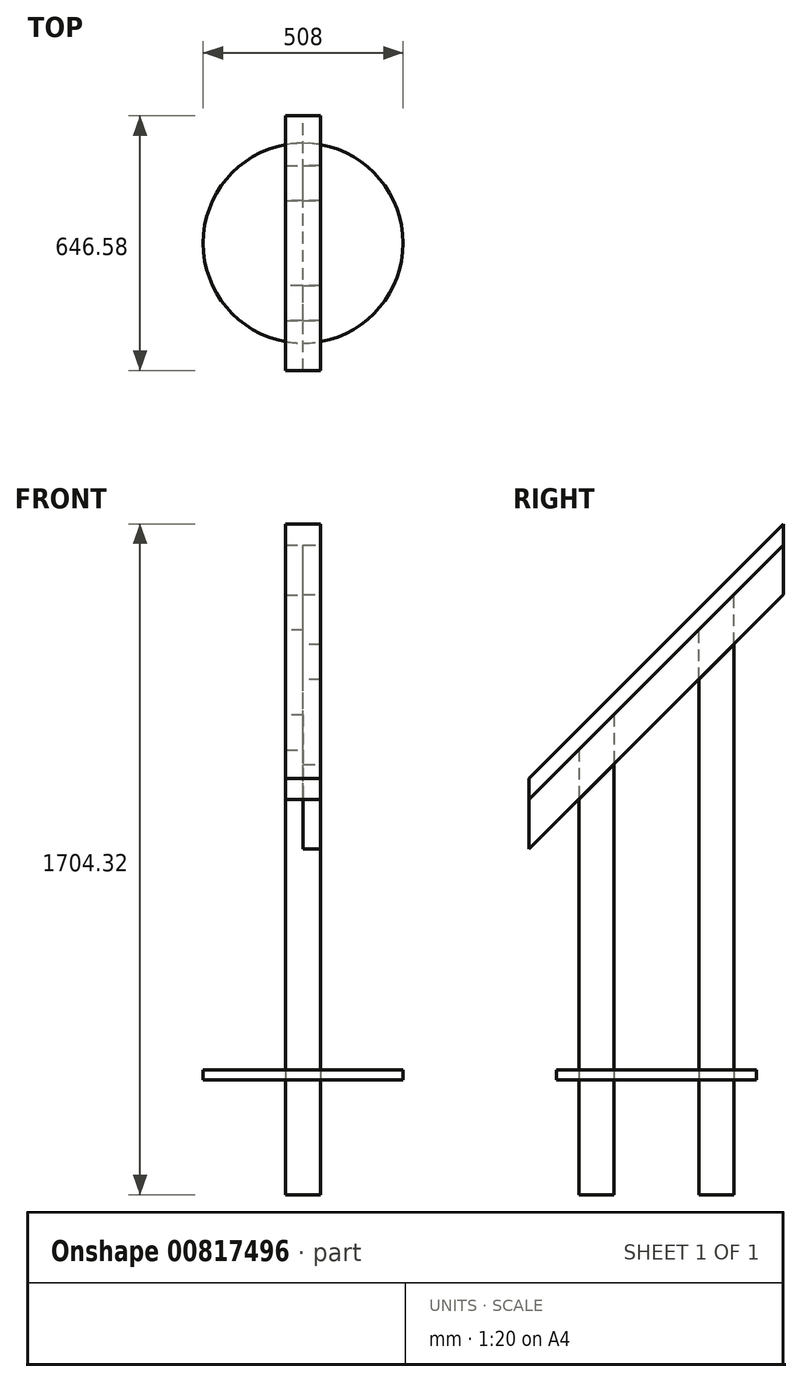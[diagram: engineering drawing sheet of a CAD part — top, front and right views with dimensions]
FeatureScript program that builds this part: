
annotation { "Feature Type Name" : "Feature", "Feature Type Description" : "" }
export const myFeature = defineFeature(function(context is Context, id is Id, definition is map)
    precondition{}
    {
        {
            var Q0;
            Q0=qCreatedBy(makeId("Top.planeOp"),FACE);
            var sketch = newSketch(context, id + "F0", { "sketchPlane" : qUnion([Q0])});
            skCircle(sketch, "E0", {"center": v(0, 0) * mm, "radius": 254 * mm});
            skCircle(sketch, "E1", {"center": v(0, 152.4) * mm, "radius": 62.86 * mm, "construction": true});
            skCircle(sketch, "E2", {"center": v(0, -152.4) * mm, "radius": 62.86 * mm, "construction": true});
            skLineSegment(sketch, "E3.bottom", {"start": v(-44.45, 107.95) * mm, "end": v(44.45, 107.95) * mm});
            skLineSegment(sketch, "E3.top", {"start": v(-44.45, 196.85) * mm, "end": v(44.45, 196.85) * mm});
            skLineSegment(sketch, "E3.left", {"start": v(-44.45, 107.95) * mm, "end": v(-44.45, 196.85) * mm});
            skLineSegment(sketch, "E3.right", {"start": v(44.45, 107.95) * mm, "end": v(44.45, 196.85) * mm});
            skLineSegment(sketch, "E4.bottom", {"start": v(44.45, -107.95) * mm, "end": v(-44.45, -107.95) * mm});
            skLineSegment(sketch, "E4.top", {"start": v(44.45, -196.85) * mm, "end": v(-44.45, -196.85) * mm});
            skLineSegment(sketch, "E4.left", {"start": v(44.45, -107.95) * mm, "end": v(44.45, -196.85) * mm});
            skLineSegment(sketch, "E4.right", {"start": v(-44.45, -107.95) * mm, "end": v(-44.45, -196.85) * mm});
            skCircle(sketch, "E5", {"center": v(0, 0) * mm, "radius": 152.4 * mm, "construction": true});
            skSolve(sketch);
        }
        {
            var Q0;
            Q0=makeQuery(id+"F0.imprint","IMPRINT",FACE,{"disambiguationData":[TD([[makeQuery(id+"F0.imprint","IMPRINT",EDGE,{"derivedFrom":sQuery(id+"F0.wireOp",EDGE,"E3.bottom")}),1.0]])]});
            extrude(context, id + "F1", {"entities" : qUnion([Q0]), "depth" : 1219.2 * mm, "offsetDistance" : 25.4 * mm, "hasSecondDirection" : true, "secondDirectionOppositeDirection" : true, "secondDirectionDepth" : 304.8 * mm});
        }
        {
            var Q0;
            Q0=makeQuery(id+"F0.imprint","IMPRINT",FACE,{"disambiguationData":[TD([[makeQuery(id+"F0.imprint","IMPRINT",EDGE,{"derivedFrom":sQuery(id+"F0.wireOp",EDGE,"E4.bottom")}),1.0]])]});
            extrude(context, id + "F2", {"entities" : qUnion([Q0]), "depth" : 914.4 * mm, "offsetDistance" : 25.4 * mm, "hasSecondDirection" : true, "secondDirectionOppositeDirection" : true, "secondDirectionDepth" : 304.8 * mm});
        }
        {
            var Q0;
            Q0=makeQuery(id+"F0.imprint","IMPRINT",FACE,{"disambiguationData":[TD([[makeQuery(id+"F0.imprint","IMPRINT",EDGE,{"derivedFrom":sQuery(id+"F0.wireOp",EDGE,"E0")}),1.0]])]});
            extrude(context, id + "F3", {"entities" : qUnion([Q0]), "endBound" : BoundingType.SYMMETRIC, "depth" : 25.4 * mm, "offsetDistance" : 25.4 * mm});
        }
        {
            var Q0;
            Q0=qCreatedBy(makeId("Right.planeOp"),FACE);
            var sketch = newSketch(context, id + "F4", { "sketchPlane" : qUnion([Q0])});
            skLineSegment(sketch, "E6.0.0", {"start": v(-196.85, -304.8) * mm, "end": v(-107.95, -304.8) * mm, "construction": true});
            skLineSegment(sketch, "E6.0.1", {"start": v(-107.95, -304.8) * mm, "end": v(-107.95, 914.4) * mm, "construction": true});
            skLineSegment(sketch, "E6.0.2", {"start": v(-107.95, 914.4) * mm, "end": v(-196.85, 914.4) * mm, "construction": true});
            skLineSegment(sketch, "E6.0.3", {"start": v(-196.85, 914.4) * mm, "end": v(-196.85, -304.8) * mm, "construction": true});
            skLineSegment(sketch, "E6.1.0", {"start": v(107.95, -304.8) * mm, "end": v(196.85, -304.8) * mm, "construction": true});
            skLineSegment(sketch, "E6.1.1", {"start": v(196.85, -304.8) * mm, "end": v(196.85, 1219.2) * mm, "construction": true});
            skLineSegment(sketch, "E6.1.2", {"start": v(196.85, 1219.2) * mm, "end": v(107.95, 1219.2) * mm, "construction": true});
            skLineSegment(sketch, "E6.1.3", {"start": v(107.95, 1219.2) * mm, "end": v(107.95, -304.8) * mm, "construction": true});
            skLineSegment(sketch, "E7", {"start": v(-323.29, 699.06) * mm, "end": v(323.29, 1345.64) * mm});
            skArc(sketch, "E8", {"start": v(323.29, 1345.64) * mm, "mid": v(-323.29, 1345.64) * mm, "end": v(-323.29, 699.06) * mm, "construction": true});
            skLineSegment(sketch, "E9", {"start": v(-323.29, 787.96) * mm, "end": v(-323.29, 573.34) * mm, "construction": true});
            skLineSegment(sketch, "E10", {"start": v(-323.29, 573.34) * mm, "end": v(323.29, 1219.92) * mm, "construction": true});
            skLineSegment(sketch, "E11", {"start": v(323.29, 1219.92) * mm, "end": v(323.29, 1434.54) * mm, "construction": true});
            skLineSegment(sketch, "E12", {"start": v(-323.29, 787.96) * mm, "end": v(323.29, 1434.54) * mm, "construction": true});
            skLineSegment(sketch, "E13", {"start": v(323.29, 1399.52) * mm, "end": v(-323.29, 752.94) * mm, "construction": true});
            skSolve(sketch);
        }
        {
            var Q0;
            Q0=qCreatedBy(makeId("Front.planeOp"),FACE);
            var Q1;
            Q1=sQuery(id+"F4.wireOp",EDGE,"E9");
            cPlane(context, id + "F5", {"entities" : qUnion([Q0, Q1]), "cplaneType" : CPlaneType.LINE_ANGLE, "offset" : 25.4 * mm, "angle" : 0 * degree, "width" : 152.4 * mm, "height" : 152.4 * mm});
        }
        {
            var Q0;
            Q0=qCreatedBy(id+"F5.planeOp",FACE);
            var sketch = newSketch(context, id + "F6", { "sketchPlane" : qUnion([Q0])});
            skLineSegment(sketch, "E14.0", {"start": v(0, 787.96) * mm, "end": v(0, 573.34) * mm, "construction": true});
            skPoint(sketch, "E15.0", {"position": v(0, 752.94) * mm});
            skPoint(sketch, "E16.0", {"position": v(0, 699.06) * mm});
            skLineSegment(sketch, "E17.0.0", {"start": v(44.45, -304.8) * mm, "end": v(-44.45, -304.8) * mm, "construction": true});
            skLineSegment(sketch, "E17.0.1", {"start": v(-44.45, -304.8) * mm, "end": v(-44.45, 914.4) * mm, "construction": true});
            skLineSegment(sketch, "E17.0.2", {"start": v(-44.45, 914.4) * mm, "end": v(44.45, 914.4) * mm, "construction": true});
            skLineSegment(sketch, "E17.0.3", {"start": v(44.45, 914.4) * mm, "end": v(44.45, -304.8) * mm, "construction": true});
            skLineSegment(sketch, "E18.bottom", {"start": v(44.45, 787.96) * mm, "end": v(-44.45, 787.96) * mm});
            skLineSegment(sketch, "E18.top", {"start": v(44.45, 752.94) * mm, "end": v(-44.45, 752.94) * mm});
            skLineSegment(sketch, "E18.left", {"start": v(44.45, 787.96) * mm, "end": v(44.45, 752.94) * mm});
            skLineSegment(sketch, "E18.right", {"start": v(-44.45, 787.96) * mm, "end": v(-44.45, 752.94) * mm});
            skLineSegment(sketch, "E19.bottom", {"start": v(44.45, 699.06) * mm, "end": v(-44.45, 699.06) * mm});
            skLineSegment(sketch, "E19.left", {"start": v(44.45, 699.06) * mm, "end": v(44.45, 752.94) * mm});
            skLineSegment(sketch, "E19.right", {"start": v(-44.45, 699.06) * mm, "end": v(-44.45, 752.94) * mm});
            skLineSegment(sketch, "E20.bottom", {"start": v(0, 573.34) * mm, "end": v(-44.45, 573.34) * mm});
            skLineSegment(sketch, "E20.top", {"start": v(0, 699.06) * mm, "end": v(-44.45, 699.06) * mm});
            skLineSegment(sketch, "E20.left", {"start": v(0, 573.34) * mm, "end": v(0, 699.06) * mm});
            skLineSegment(sketch, "E20.right", {"start": v(-44.45, 573.34) * mm, "end": v(-44.45, 699.06) * mm});
            skSolve(sketch);
        }
        {
            var Q0;
            Q0=makeQuery(id+"F6.imprint","IMPRINT",FACE,{"disambiguationData":[TD([[makeQuery(id+"F6.imprint","IMPRINT",EDGE,{"derivedFrom":sQuery(id+"F6.wireOp",EDGE,"E18.bottom")}),1.0]])]});
            var Q1;
            Q1=makeQuery(id+"F6.imprint","IMPRINT",FACE,{"disambiguationData":[TD([[makeQuery(id+"F6.imprint","IMPRINT",EDGE,{"derivedFrom":sQuery(id+"F6.wireOp",EDGE,"E19.bottom")}),-1.0]])]});
            var Q2;
            Q2=makeQuery(id+"F6.imprint","IMPRINT",FACE,{"disambiguationData":[TD([[makeQuery(id+"F6.imprint","IMPRINT",EDGE,{"derivedFrom":sQuery(id+"F6.wireOp",EDGE,"E20.bottom")}),-1.0]])]});
            var Q3;
            Q3=sQuery(id+"F4.wireOp",EDGE,"E7");
            sweep(context, id + "F7", {"operationType" : NewBodyOperationType.REMOVE, "profiles" : qUnion([Q0, Q1, Q2]), "path" : qUnion([Q3])});
        }
        {
            var Q0;
            Q0 = qSketchRegion(id + "F4", true);
            var Q1;
            Q1=makeQuery(id+"F6.imprint","IMPRINT",FACE,{"disambiguationData":[TD([[makeQuery(id+"F6.imprint","IMPRINT",EDGE,{"derivedFrom":sQuery(id+"F6.wireOp",EDGE,"E20.bottom")}),-1.0]])]});
            var Q2;
            Q2=sQuery(id+"F4.wireOp",EDGE,"E7");
            sweep(context, id + "F8", {"profiles" : qUnion([Q0, Q1]), "path" : qUnion([Q2])});
        }
        {
            var Q0;
            Q0=makeQuery(id+"F6.imprint","IMPRINT",FACE,{"disambiguationData":[TD([[makeQuery(id+"F6.imprint","IMPRINT",EDGE,{"derivedFrom":sQuery(id+"F6.wireOp",EDGE,"E19.bottom")}),-1.0]])]});
            var Q1;
            Q1=makeQuery(id+"F8.opSweep","SWEPT_EDGE",EDGE,{"disambiguationData":[OSD([sQuery(id+"F4.wireOp",EDGE,"E7"),sQuery(id+"F6.wireOp",EDGE,"E19.right"),sQuery(id+"F6.wireOp",EDGE,"E20.top"),sQuery(id+"F6.wireOp",EDGE,"E20.right")])]});
            sweep(context, id + "F9", {"profiles" : qUnion([Q0]), "path" : qUnion([Q1])});
        }
    });
